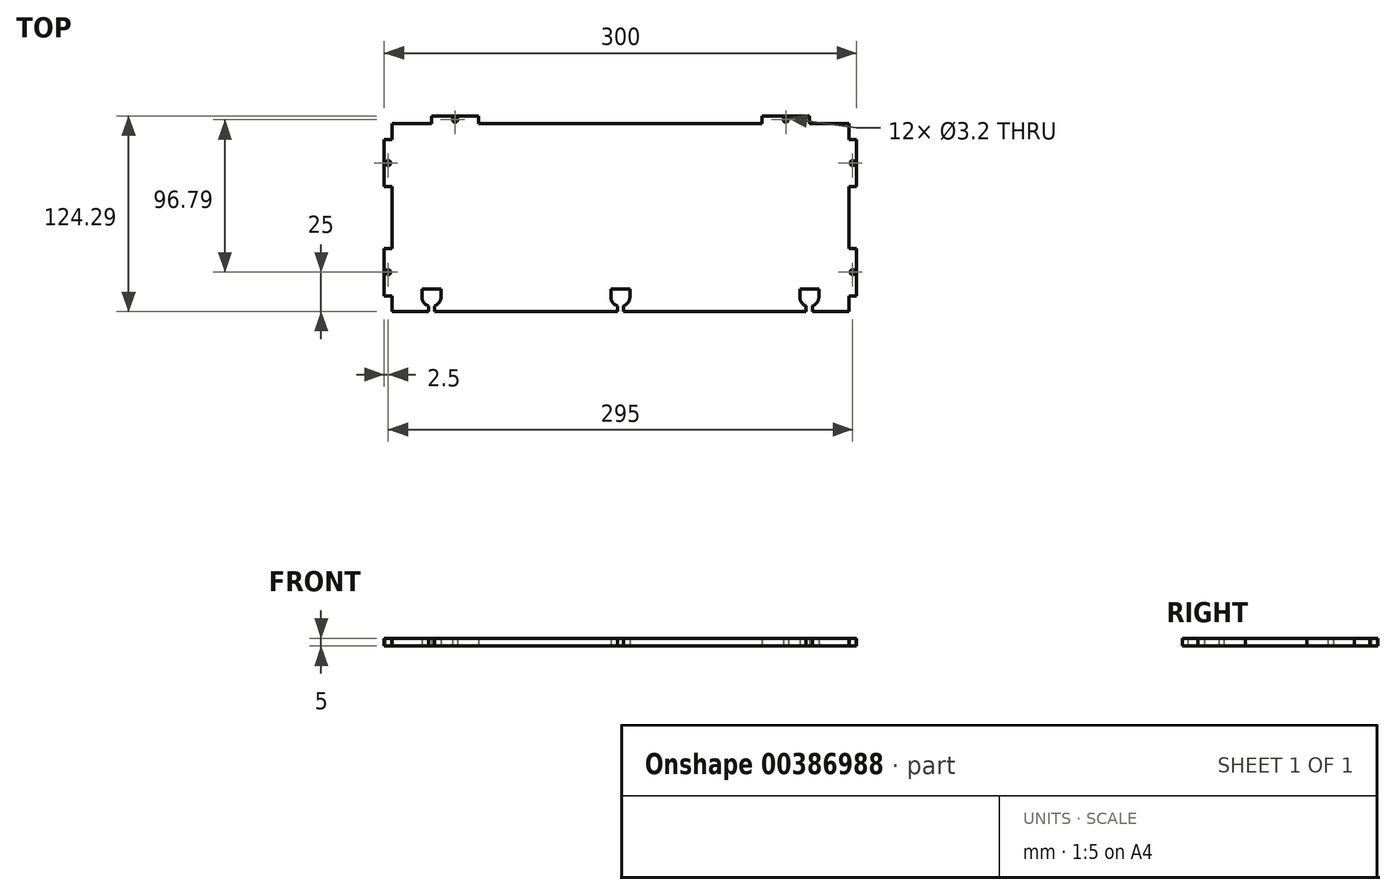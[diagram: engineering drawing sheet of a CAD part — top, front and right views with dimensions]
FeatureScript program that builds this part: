
annotation { "Feature Type Name" : "Feature", "Feature Type Description" : "" }
export const myFeature = defineFeature(function(context is Context, id is Id, definition is map)
    precondition{}
    {
        {
            var Q0;
            Q0=qCreatedBy(makeId("Top.planeOp"),FACE);
            var sketch = newSketch(context, id + "F0", { "sketchPlane" : qUnion([Q0])});
            skLineSegment(sketch, "E0.bottom", {"start": v(0, 0) * mm, "end": v(25, 0) * mm});
            skLineSegment(sketch, "E0.top", {"start": v(0, -119.29) * mm, "end": v(23, -119.29) * mm});
            skLineSegment(sketch, "E0.left", {"start": v(0, 0) * mm, "end": v(0, -10) * mm});
            skLineSegment(sketch, "E0.right", {"start": v(290, 0) * mm, "end": v(290, -10) * mm});
            skLineSegment(sketch, "E1.bottom", {"start": v(290, -109.3) * mm, "end": v(295, -109.3) * mm});
            skLineSegment(sketch, "E1.top", {"start": v(290, -79.3) * mm, "end": v(295, -79.3) * mm});
            skLineSegment(sketch, "E1.right", {"start": v(295, -109.3) * mm, "end": v(295, -79.3) * mm});
            skLineSegment(sketch, "E2.bottom", {"start": v(290, -40) * mm, "end": v(295, -40) * mm});
            skLineSegment(sketch, "E2.top", {"start": v(290, -10) * mm, "end": v(295, -10) * mm});
            skLineSegment(sketch, "E2.right", {"start": v(295, -40) * mm, "end": v(295, -10) * mm});
            skLineSegment(sketch, "E3.trimOffspring", {"start": v(290, -109.3) * mm, "end": v(290, -119.3) * mm});
            skLineSegment(sketch, "E4.trimOffspring", {"start": v(290, -40) * mm, "end": v(290, -79.3) * mm});
            skLineSegment(sketch, "E5.bottom", {"start": v(0, -10) * mm, "end": v(-5, -10) * mm});
            skLineSegment(sketch, "E5.top", {"start": v(0, -40) * mm, "end": v(-5, -40) * mm});
            skLineSegment(sketch, "E5.right", {"start": v(-5, -10) * mm, "end": v(-5, -40) * mm});
            skLineSegment(sketch, "E6.bottom", {"start": v(0, -109.3) * mm, "end": v(-5, -109.3) * mm});
            skLineSegment(sketch, "E6.top", {"start": v(0, -79.3) * mm, "end": v(-5, -79.3) * mm});
            skLineSegment(sketch, "E6.right", {"start": v(-5, -109.3) * mm, "end": v(-5, -79.3) * mm});
            skLineSegment(sketch, "E7.trimOffspring", {"start": v(0, -109.3) * mm, "end": v(0, -119.29) * mm});
            skLineSegment(sketch, "E8.trimOffspring", {"start": v(0, -40) * mm, "end": v(0, -79.3) * mm});
            skLineSegment(sketch, "E9.top", {"start": v(25, 5) * mm, "end": v(55, 5) * mm});
            skLineSegment(sketch, "E9.left", {"start": v(25, 0) * mm, "end": v(25, 5) * mm});
            skLineSegment(sketch, "E9.right", {"start": v(55, 0) * mm, "end": v(55, 5) * mm});
            skLineSegment(sketch, "E10.top", {"start": v(265, 5) * mm, "end": v(235, 5) * mm});
            skLineSegment(sketch, "E10.left", {"start": v(265, 0) * mm, "end": v(265, 5) * mm});
            skLineSegment(sketch, "E10.right", {"start": v(235, 0) * mm, "end": v(235, 5) * mm});
            skLineSegment(sketch, "E11.trimOffspring", {"start": v(265, 0) * mm, "end": v(290, 0) * mm});
            skLineSegment(sketch, "E12.trimOffspring", {"start": v(55, 0) * mm, "end": v(235, 0) * mm});
            skCircle(sketch, "E13", {"center": v(292.5, -94.3) * mm, "radius": 1.6 * mm});
            skPoint(sketch, "E13.centerSnap0", {"position": v(295, -94.3) * mm});
            skCircle(sketch, "E14", {"center": v(292.5, -25) * mm, "radius": 1.6 * mm});
            skPoint(sketch, "E14.centerSnap0", {"position": v(295, -25) * mm});
            skCircle(sketch, "E15", {"center": v(-2.5, -94.3) * mm, "radius": 1.6 * mm});
            skPoint(sketch, "E15.centerSnap0", {"position": v(-5, -94.3) * mm});
            skCircle(sketch, "E16", {"center": v(-2.5, -25) * mm, "radius": 1.6 * mm});
            skPoint(sketch, "E16.centerSnap0", {"position": v(-5, -25) * mm});
            skCircle(sketch, "E17", {"center": v(40, 2.5) * mm, "radius": 1.6 * mm});
            skPoint(sketch, "E17.centerSnap0", {"position": v(40, 5) * mm});
            skCircle(sketch, "E18", {"center": v(250, 2.5) * mm, "radius": 1.6 * mm});
            skPoint(sketch, "E18.centerSnap0", {"position": v(250, 5) * mm});
            skPoint(sketch, "E19", {"position": v(292.5, -40) * mm});
            skPoint(sketch, "E20", {"position": v(292.5, -109.3) * mm});
            skPoint(sketch, "E21", {"position": v(265, 2.5) * mm});
            skPoint(sketch, "E22", {"position": v(-2.5, -79.3) * mm});
            skPoint(sketch, "E23", {"position": v(-2.5, -10) * mm});
            skPoint(sketch, "E24", {"position": v(55, 2.5) * mm});
            skLineSegment(sketch, "E25", {"start": v(19, -105.13) * mm, "end": v(31, -105.13) * mm});
            skLineSegment(sketch, "E26", {"start": v(19, -105.13) * mm, "end": v(19, -110.13) * mm});
            skLineSegment(sketch, "E27", {"start": v(31, -105.13) * mm, "end": v(31, -110.13) * mm});
            skLineSegment(sketch, "E28", {"start": v(23, -119.3) * mm, "end": v(23, -115.8) * mm});
            skLineSegment(sketch, "E29", {"start": v(27, -119.3) * mm, "end": v(27, -115.8) * mm});
            skArc(sketch, "E30", {"start": v(19, -110.13) * mm, "mid": v(20.1, -113.6) * mm, "end": v(23, -115.8) * mm});
            skArc(sketch, "E31.trimOffspring", {"start": v(27, -115.8) * mm, "mid": v(29.9, -113.6) * mm, "end": v(31, -110.13) * mm});
            skLineSegment(sketch, "E32.0", {"start": v(27, -115.8) * mm, "end": v(27, -119.3) * mm, "construction": true});
            skLineSegment(sketch, "E33.0", {"start": v(19, -110.13) * mm, "end": v(31, -110.13) * mm, "construction": true});
            skLineSegment(sketch, "E34", {"start": v(259, -105.13) * mm, "end": v(271, -105.13) * mm});
            skLineSegment(sketch, "E35", {"start": v(259, -105.13) * mm, "end": v(259, -110.13) * mm});
            skLineSegment(sketch, "E36", {"start": v(271, -105.13) * mm, "end": v(271, -110.13) * mm});
            skLineSegment(sketch, "E37", {"start": v(263, -119.29) * mm, "end": v(263, -115.8) * mm});
            skLineSegment(sketch, "E38", {"start": v(267, -119.29) * mm, "end": v(267, -115.8) * mm});
            skArc(sketch, "E39", {"start": v(259, -110.13) * mm, "mid": v(260.1, -113.6) * mm, "end": v(263, -115.8) * mm});
            skArc(sketch, "E40.trimOffspring", {"start": v(267, -115.8) * mm, "mid": v(269.9, -113.6) * mm, "end": v(271, -110.13) * mm});
            skLineSegment(sketch, "E41.0", {"start": v(267, -115.8) * mm, "end": v(267, -119.29) * mm, "construction": true});
            skLineSegment(sketch, "E42.0", {"start": v(259, -110.13) * mm, "end": v(271, -110.13) * mm, "construction": true});
            skLineSegment(sketch, "E43.trimOffspring", {"start": v(267, -119.29) * mm, "end": v(290, -119.29) * mm});
            skLineSegment(sketch, "E44.trimOffspring", {"start": v(27, -119.29) * mm, "end": v(143, -119.29) * mm});
            skLineSegment(sketch, "E45", {"start": v(139, -105.13) * mm, "end": v(151, -105.13) * mm});
            skLineSegment(sketch, "E46", {"start": v(139, -105.13) * mm, "end": v(139, -110.13) * mm});
            skLineSegment(sketch, "E47", {"start": v(151, -105.13) * mm, "end": v(151, -110.13) * mm});
            skLineSegment(sketch, "E48", {"start": v(143, -119.29) * mm, "end": v(143, -115.79) * mm});
            skLineSegment(sketch, "E49", {"start": v(147, -119.29) * mm, "end": v(147, -115.79) * mm});
            skArc(sketch, "E50", {"start": v(139, -110.13) * mm, "mid": v(140.1, -113.6) * mm, "end": v(143, -115.79) * mm});
            skArc(sketch, "E51.trimOffspring", {"start": v(147, -115.79) * mm, "mid": v(149.9, -113.6) * mm, "end": v(151, -110.13) * mm});
            skLineSegment(sketch, "E52.0", {"start": v(147, -115.79) * mm, "end": v(147, -119.29) * mm, "construction": true});
            skLineSegment(sketch, "E53.0", {"start": v(139, -110.13) * mm, "end": v(151, -110.13) * mm, "construction": true});
            skLineSegment(sketch, "E54.trimOffspring", {"start": v(147, -119.29) * mm, "end": v(263, -119.29) * mm});
            skPoint(sketch, "E55", {"position": v(145, 0) * mm});
            skSolve(sketch);
        }
        {
            var Q0;
            Q0=makeQuery(id+"F0.imprint","IMPRINT",FACE,{"disambiguationData":[TD([[makeQuery(id+"F0.imprint","IMPRINT",EDGE,{"derivedFrom":sQuery(id+"F0.wireOp",EDGE,"E0.bottom")}),-1.0]])]});
            extrude(context, id + "F1", {"entities" : qUnion([Q0]), "depth" : 5 * mm});
        }
    });
